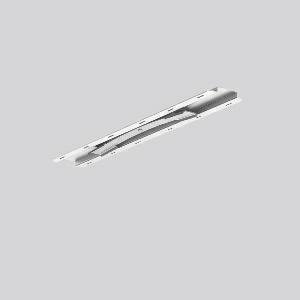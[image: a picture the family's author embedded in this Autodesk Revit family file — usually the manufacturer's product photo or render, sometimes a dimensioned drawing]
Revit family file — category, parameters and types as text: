
# Revit family: linedo_pendelset_verbinder_982680_000_81c2
name_source: partatom
category: Lighting Fixtures
units: mm (PartAtom-declared; Revit-internal decimal feet)

## family parameters
Cut with Voids When Loaded = No
Host = Face
Light Source = No
Part Type = Normal
Room Calculation Point = No
Round Connector Dimension = Use Diameter
Shared = No

## types (1)
- LINEDO Pendelset Verbinder
    Apparent Load = 0 VA
    Default Elevation = 1800 mm
    Description = Connector for suspended installation. Metal lever galvanised to mechanically connect 2 LINEDO suspended modules. A connector must be placed at each joint between modules.
Colour: zinc plated
Length: 300 mm
Width: 48 mm
Height: 9 mm
Weight: 182 g
    Height = 9 mm  [stored 0.0295276 ft]
    Lamp = 0 x
    Length = 300 mm
    Luminous efficacy = 0 lm/W
    Manufacturer = RZB
    ModVariant = No
    Model = 982680.000
    Mounting Place = Ceiling
    Mounting Type = Surface mounted
    Number of Poles = 1
    OnlyDefault = Yes
    Power Factor = 1
    Product Name = LINEDO Pendelset Verbinder
    Product group = Surface mounted continuous line luminaire system
    ProductGroupID = 310
    Protection Class = Protection class
    Protection Degree = Degree of protection
    RLX_Detail_Level = 1
    RLX_Emergency_Light_Flux = 0 lm
    RLX_Emergency_Type = 0
    RLX_Emergency_Type_DB = No
    RlxData = <blob elided: 11341 chars, md5=5012ad3a>
    Standby Power = 0 W
    System Light Flux = 0 lm
    System Power = 0 W
    Type Comments = Product without accessories
    Type Image = 982680.000.jpg
    URL = http://relux.com
    VarID = ---
    Voltage = 0 V
    Weight = 0.00 kg
    Width = 49 mm

note: [stored X ft] marks values corroborated as IEEE doubles in the binary element streams (Revit-internal decimal feet)

## geometry (parser evidence)
native form markers: Sweep x8
no freeform markers — native parametric forms only
